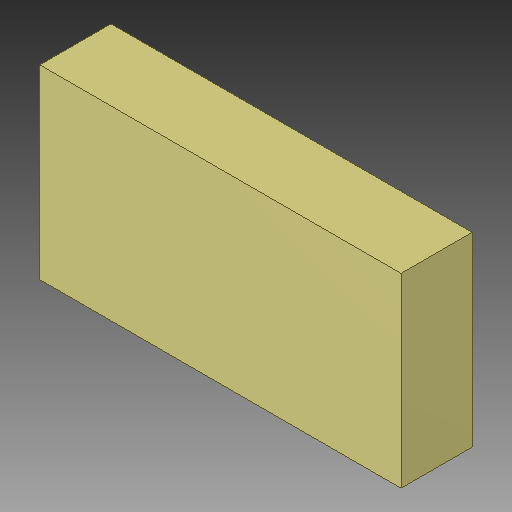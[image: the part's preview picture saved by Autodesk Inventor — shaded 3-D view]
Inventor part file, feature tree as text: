
AUTODESK INVENTOR PART (.ipt)
format: ipt  version: 2019 (Build 230136000, 136)  size: 86,016 bytes
history: native  units: in
note: dims shown in document units (in); Inventor stores cm internally (conversion verified against a paired STEP export)
features: extrude x1, other x1
ambient origin geometry x8: Origin, YZ Plane, XZ Plane, XY Plane, X Axis, Y Axis, Z Axis, Center Point
bodies: Solid1 (feature_tree)
feature tree (2):
  extrude  "Extrusion1"  Depth=0.0394in TaperAngle=0.0deg
  other  "1X02, 1X02_8"
